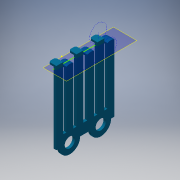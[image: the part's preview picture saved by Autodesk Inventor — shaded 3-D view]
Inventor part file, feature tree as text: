
AUTODESK INVENTOR PART (.ipt)
format: ipt  version: 2016 (Build 200138000, 138)  size: 410,624 bytes
history: native  units: in
note: dims shown in document units (in); Inventor stores cm internally (conversion verified against a paired STEP export)
features: sketch x14, extrude x13, projected_geometry x9, reference x8, plane x6, fillet x2, mirror x1, imported_body x1, boolean_combine x1
ambient origin geometry x8: Origin, YZ Plane, XZ Plane, XY Plane, X Axis, Y Axis, Z Axis, Center Point
bodies: Solid1 (feature_tree), Solid2 (feature_tree)
feature tree (55):
  extrude  "Extrusion1"  Depth=0.0079in
  sketch  "Sketch2"  dims[d11=0.0079in d12=0.052in d13=0.052in]
  plane  "Work Plane1"
  plane  "Work Plane2"
  extrude  "Extrusion2"  Depth=0.052in
  fillet  "Fillet1"  Radius=0.052in
  extrude  "Extrusion3"  Depth=0.052in
  sketch  "Sketch4"  dims[d16=0.025in d17=0.025in d18=0.0197in d19=0.0in]
  plane  "Work Plane3"
  extrude  "Extrusion5"  Depth=0.025in
  fillet  "Fillet3"  Radius=0.0197in
  sketch  "Sketch6"  dims[d23=0.3937in d24=0.0in d25=0.0787in]
  plane  "Work Plane4"
  mirror  "Mirror1"
  extrude  "Extrusion6"  Depth=0.0197in
  plane  "Work Plane5"
  extrude  "Extrusion7"  Depth=0.0787in
  extrude  "Extrusion8"  Depth=0.0394in
  extrude  "Extrusion9"  Depth=0.0394in TaperAngle=0.0deg
  extrude  "Extrusion10"  TaperAngle=90.0deg  [1 undecoded]
  extrude  "Extrusion11"  Depth=0.0394in TaperAngle=0.0deg
  extrude  "Extrusion12"  Depth=0.0492in TaperAngle=0.0deg
  extrude  "Extrusion13"  Depth=0.0394in TaperAngle=0.0deg
  imported_body  "Base1"
  boolean_combine  "Combine1"
  sketch  "Sketch14"  dims[d55=1.0in d56=0.0in]
  plane  "Work Plane6"
  extrude  "Extrusion14"  Depth=0.0157in TaperAngle=0.0deg
  sketch  "Sketch1"  dims[d9=0.0079in d10=0.0079in]
  reference  "Reference1"
  reference  "Reference2"
  reference  "Reference3"
  reference  "Reference4"
  reference  "Reference5"
  sketch  "Sketch3"  dims[d14=0.052in d15=0.0079in]
  projected_geometry  "Projected Loop1"
  projected_geometry  "Projected Loop2"
  projected_geometry  "Projected Loop3"
  projected_geometry  "Projected Loop4"
  projected_geometry  "Projected Loop5"
  projected_geometry  "Projected Loop6"
  sketch  "Sketch5"  dims[d20=0.0197in d21=0.0in d22=0.0197in]
  reference  "Reference6"
  reference  "Reference7"
  reference  "Reference8"
  sketch  "Sketch7"  dims[d29=0.0394in d30=0.0394in]
  sketch  "Sketch8"  dims[d31=0.1181in d32=0.0394in d33=0.0in]
  sketch  "Sketch9"  dims[d34=0.0157in d36=90.0deg]
  projected_geometry  "Projected Loop7"
  projected_geometry  "Projected Loop8"
  sketch  "Sketch10"  dims[d37=0.0394in d38=0.0in d39=0.0492in d40=0.0in]
  sketch  "Sketch11"  dims[d41=0.0in d42=0.0in d43=0.0492in d44=0.0in]
  sketch  "Sketch12"  dims[d45=0.0394in d46=0.0in d48=0.0394in d49=0.0in]
  sketch  "Sketch13"  dims[d50=0.0394in d51=0.0in d52=0.0157in d53=0.0in]
  projected_geometry  "Projected Loop9"
note: 1 required parameter value undecoded (feature->parameter linkage not recoverable at this tier; creation-order binding heuristic only, values carry confidence <= 0.55)
